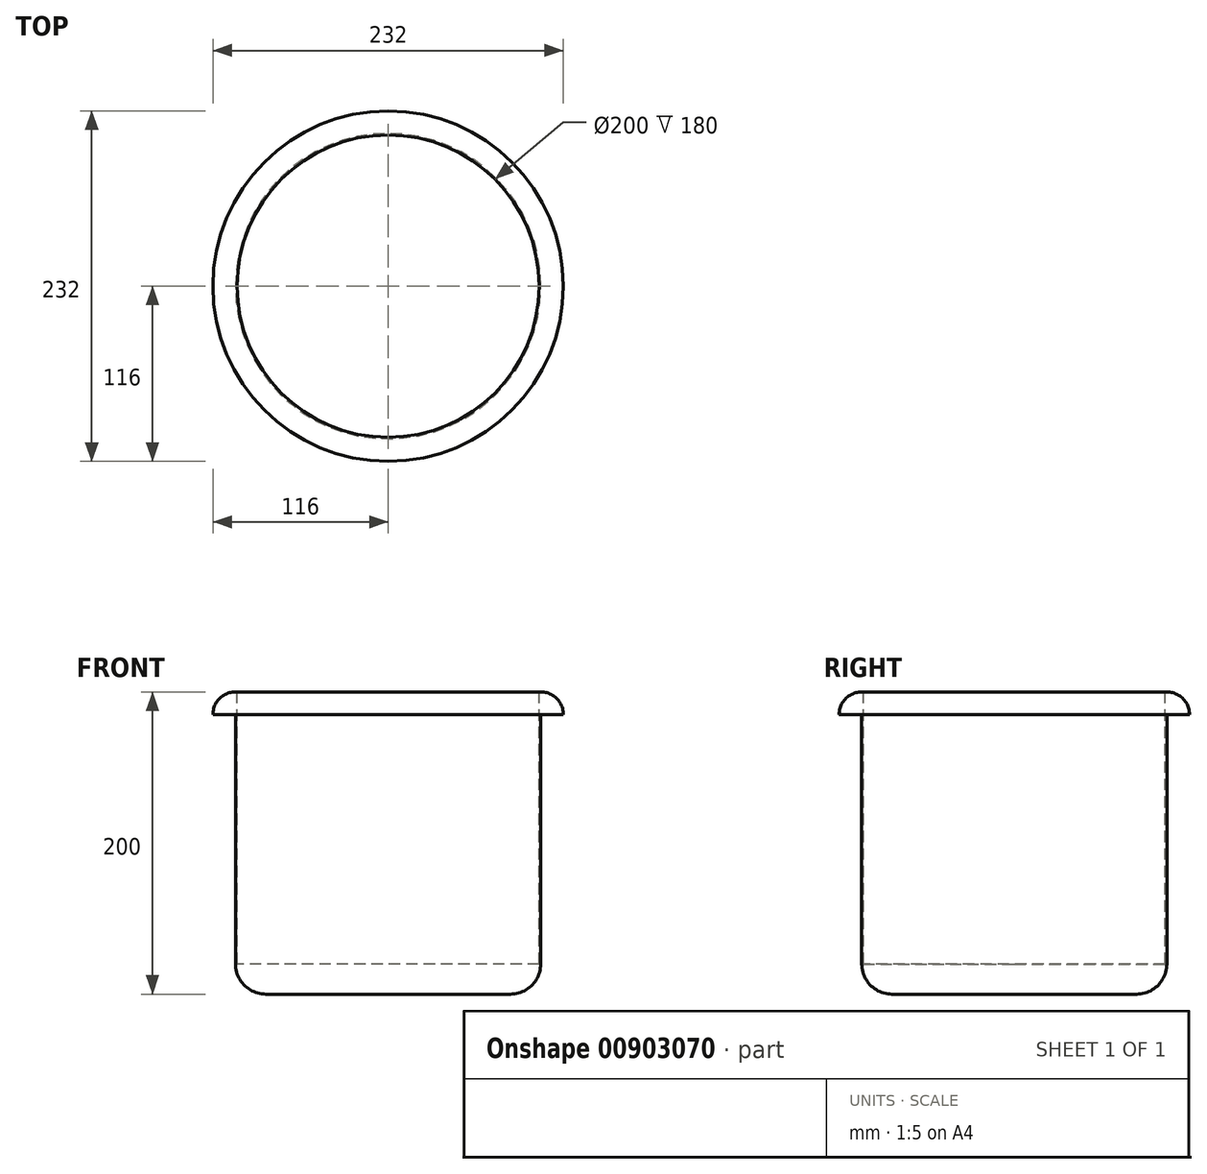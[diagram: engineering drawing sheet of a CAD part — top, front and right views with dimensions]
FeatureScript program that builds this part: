
annotation { "Feature Type Name" : "Feature", "Feature Type Description" : "" }
export const myFeature = defineFeature(function(context is Context, id is Id, definition is map)
    precondition{}
    {
        {
            var Q0;
            Q0=qCreatedBy(makeId("Top.planeOp"),FACE);
            var sketch = newSketch(context, id + "F0", { "sketchPlane" : qUnion([Q0])});
            skCircle(sketch, "E0", {"center": v(0, 0) * mm, "radius": 101 * mm});
            skSolve(sketch);
        }
        {
            var Q0;
            Q0=makeQuery(id+"F0.imprint","IMPRINT",FACE,{"disambiguationData":[TD([[makeQuery(id+"F0.imprint","IMPRINT",EDGE,{"derivedFrom":sQuery(id+"F0.wireOp",EDGE,"E0")}),1.0]])]});
            extrude(context, id + "F1", {"entities" : qUnion([Q0]), "depth" : 200 * mm, "offsetDistance" : 25 * mm});
        }
        {
            var Q0;
            Q0=makeQuery(id+"F1.opExtrude","CAP_FACE",FACE,{"disambiguationData":[OSD([sQuery(id+"F0.wireOp",EDGE,"E0")])],"isStart":true});
            fillet(context, id + "F2", {"entities" : qUnion([Q0]), "radius" : 20 * mm, "tangentPropagation" : true, "allowEdgeOverflow" : false});
        }
        {
            var Q0;
            Q0=makeQuery(id+"F1.opExtrude","CAP_FACE",FACE,{"disambiguationData":[OSD([sQuery(id+"F0.wireOp",EDGE,"E0")])],"isStart":false});
            var sketch = newSketch(context, id + "F3", { "sketchPlane" : qUnion([Q0])});
            skCircle(sketch, "E1", {"center": v(0, 0) * mm, "radius": 100 * mm});
            skSolve(sketch);
        }
        {
            var Q0;
            Q0=makeQuery(id+"F3.imprint","IMPRINT",FACE,{"disambiguationData":[TD([[makeQuery(id+"F3.imprint","IMPRINT",EDGE,{"derivedFrom":sQuery(id+"F3.wireOp",EDGE,"E1")}),1.0]])]});
            extrude(context, id + "F4", {"entities" : qUnion([Q0]), "operationType" : NewBodyOperationType.REMOVE, "oppositeDirection" : true, "depth" : 180 * mm, "offsetDistance" : 25 * mm});
        }
        {
            var Q0;
            Q0=makeQuery(id+"F1.opExtrude","CAP_FACE",FACE,{"disambiguationData":[OSD([sQuery(id+"F0.wireOp",EDGE,"E0")])],"isStart":false});
            var sketch = newSketch(context, id + "F5", { "sketchPlane" : qUnion([Q0])});
            skCircle(sketch, "E2", {"center": v(0, 0) * mm, "radius": 116 * mm});
            skSolve(sketch);
        }
        {
            var Q0;
            Q0=makeQuery(id+"F5.imprint","IMPRINT",FACE,{"disambiguationData":[TD([[makeQuery(id+"F5.imprint","IMPRINT",EDGE,{"derivedFrom":sQuery(id+"F5.wireOp",EDGE,"E2")}),1.0]])]});
            extrude(context, id + "F6", {"entities" : qUnion([Q0]), "operationType" : NewBodyOperationType.ADD, "oppositeDirection" : true, "depth" : 15 * mm, "offsetDistance" : 25 * mm});
        }
        {
            var Q0;
            Q0=makeQuery(id+"F6.opExtrude","CAP_EDGE",EDGE,{"disambiguationData":[OSD([sQuery(id+"F5.wireOp",EDGE,"E2")])],"isStart":true});
            fillet(context, id + "F7", {"entities" : qUnion([Q0]), "radius" : 15 * mm, "tangentPropagation" : true, "allowEdgeOverflow" : false});
        }
    });
